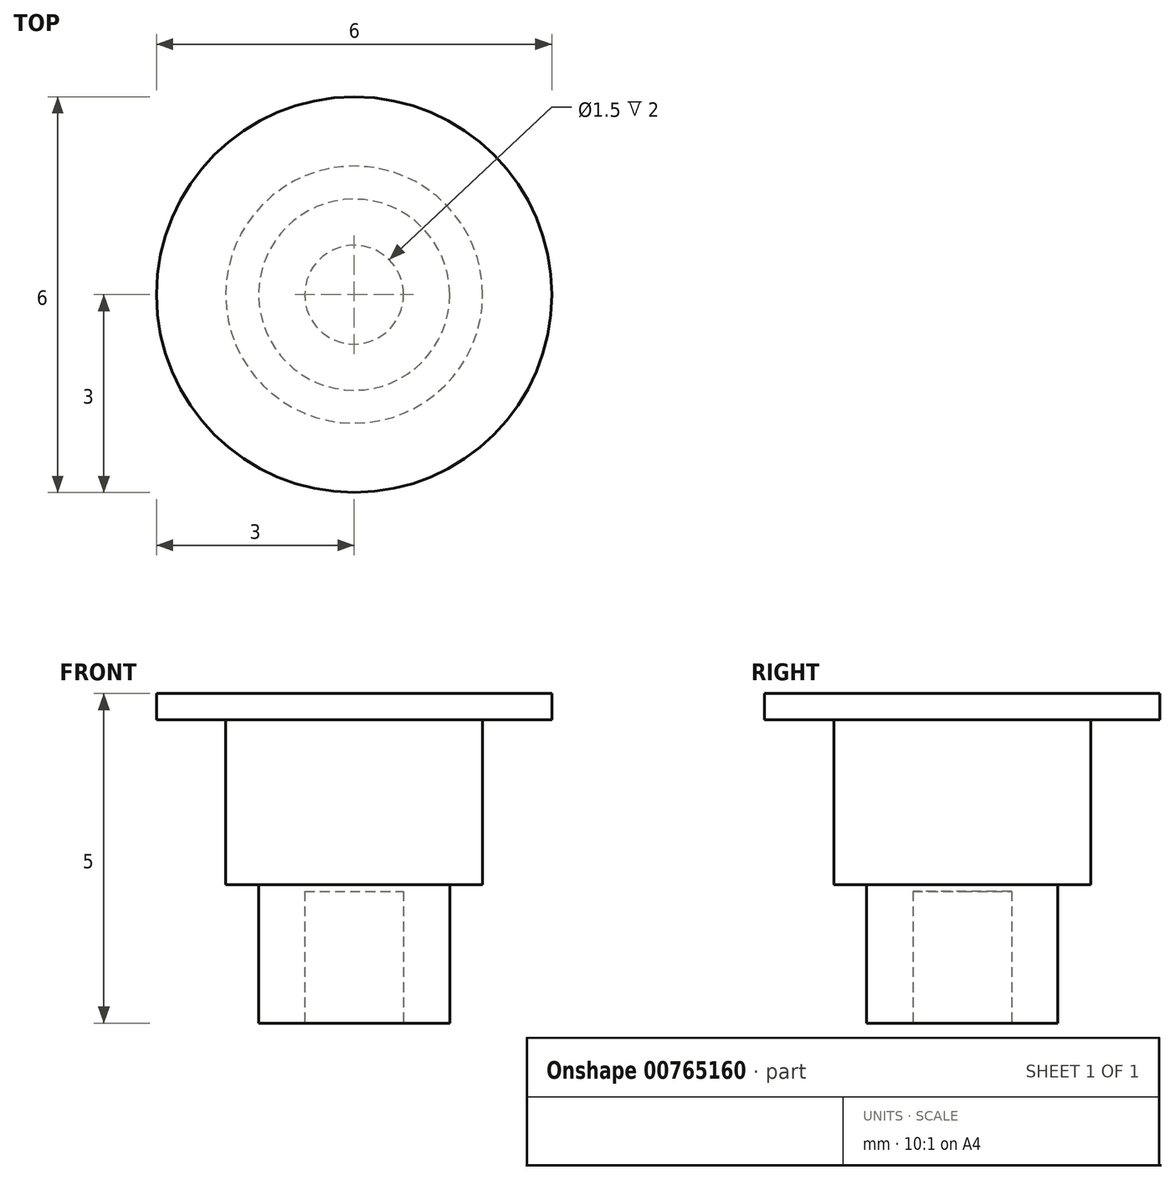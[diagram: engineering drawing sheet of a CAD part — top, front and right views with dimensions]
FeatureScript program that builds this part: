
annotation { "Feature Type Name" : "Feature", "Feature Type Description" : "" }
export const myFeature = defineFeature(function(context is Context, id is Id, definition is map)
    precondition{}
    {
        {
            var Q0;
            Q0=qCreatedBy(makeId("Top.planeOp"),FACE);
            var sketch = newSketch(context, id + "F0", { "sketchPlane" : qUnion([Q0])});
            skCircle(sketch, "E0", {"center": v(0, 0) * mm, "radius": 3 * mm});
            skSolve(sketch);
        }
        {
            var Q0;
            Q0 = qSketchRegion(id + "F0", true);
            extrude(context, id + "F1", {"entities" : qUnion([Q0]), "depth" : 0.4 * mm, "offsetDistance" : 25 * mm});
        }
        {
            var Q0;
            Q0=makeQuery(id+"F1.opExtrude","CAP_FACE",FACE,{"disambiguationData":[OSD([sQuery(id+"F0.wireOp",EDGE,"E0")])],"isStart":true});
            var sketch = newSketch(context, id + "F2", { "sketchPlane" : qUnion([Q0])});
            skCircle(sketch, "E1", {"center": v(0, 0) * mm, "radius": 1.95 * mm});
            skSolve(sketch);
        }
        {
            var Q0;
            Q0=makeQuery(id+"F2.imprint","IMPRINT",FACE,{"disambiguationData":[TD([[makeQuery(id+"F2.imprint","IMPRINT",EDGE,{"derivedFrom":sQuery(id+"F2.wireOp",EDGE,"E1")}),1.0]])]});
            extrude(context, id + "F3", {"entities" : qUnion([Q0]), "operationType" : NewBodyOperationType.ADD, "depth" : 2.5 * mm, "offsetDistance" : 25 * mm});
        }
        {
            var Q0;
            Q0=makeQuery(id+"F3.opExtrude","CAP_FACE",FACE,{"disambiguationData":[OSD([sQuery(id+"F2.wireOp",EDGE,"E1")])],"isStart":false});
            var sketch = newSketch(context, id + "F4", { "sketchPlane" : qUnion([Q0])});
            skCircle(sketch, "E2", {"center": v(0, 0) * mm, "radius": 1.45 * mm});
            skSolve(sketch);
        }
        {
            var Q0;
            Q0=makeQuery(id+"F4.imprint","IMPRINT",FACE,{"disambiguationData":[TD([[makeQuery(id+"F4.imprint","IMPRINT",EDGE,{"derivedFrom":sQuery(id+"F4.wireOp",EDGE,"E2")}),1.0]])]});
            extrude(context, id + "F5", {"entities" : qUnion([Q0]), "operationType" : NewBodyOperationType.ADD, "depth" : (5 - 2.9) * mm, "offsetDistance" : 25 * mm});
        }
        {
            var Q0;
            Q0=makeQuery(id+"F5.opExtrude","CAP_FACE",FACE,{"disambiguationData":[OSD([sQuery(id+"F4.wireOp",EDGE,"E2")])],"isStart":false});
            var sketch = newSketch(context, id + "F6", { "sketchPlane" : qUnion([Q0])});
            skCircle(sketch, "E3", {"center": v(0, 0) * mm, "radius": 0.75 * mm});
            skSolve(sketch);
        }
        {
            var Q0;
            Q0=makeQuery(id+"F6.imprint","IMPRINT",FACE,{"disambiguationData":[TD([[makeQuery(id+"F6.imprint","IMPRINT",EDGE,{"derivedFrom":sQuery(id+"F6.wireOp",EDGE,"E3")}),1.0]])]});
            extrude(context, id + "F7", {"entities" : qUnion([Q0]), "operationType" : NewBodyOperationType.REMOVE, "oppositeDirection" : true, "depth" : 2 * mm, "offsetDistance" : 25 * mm});
        }
    });
